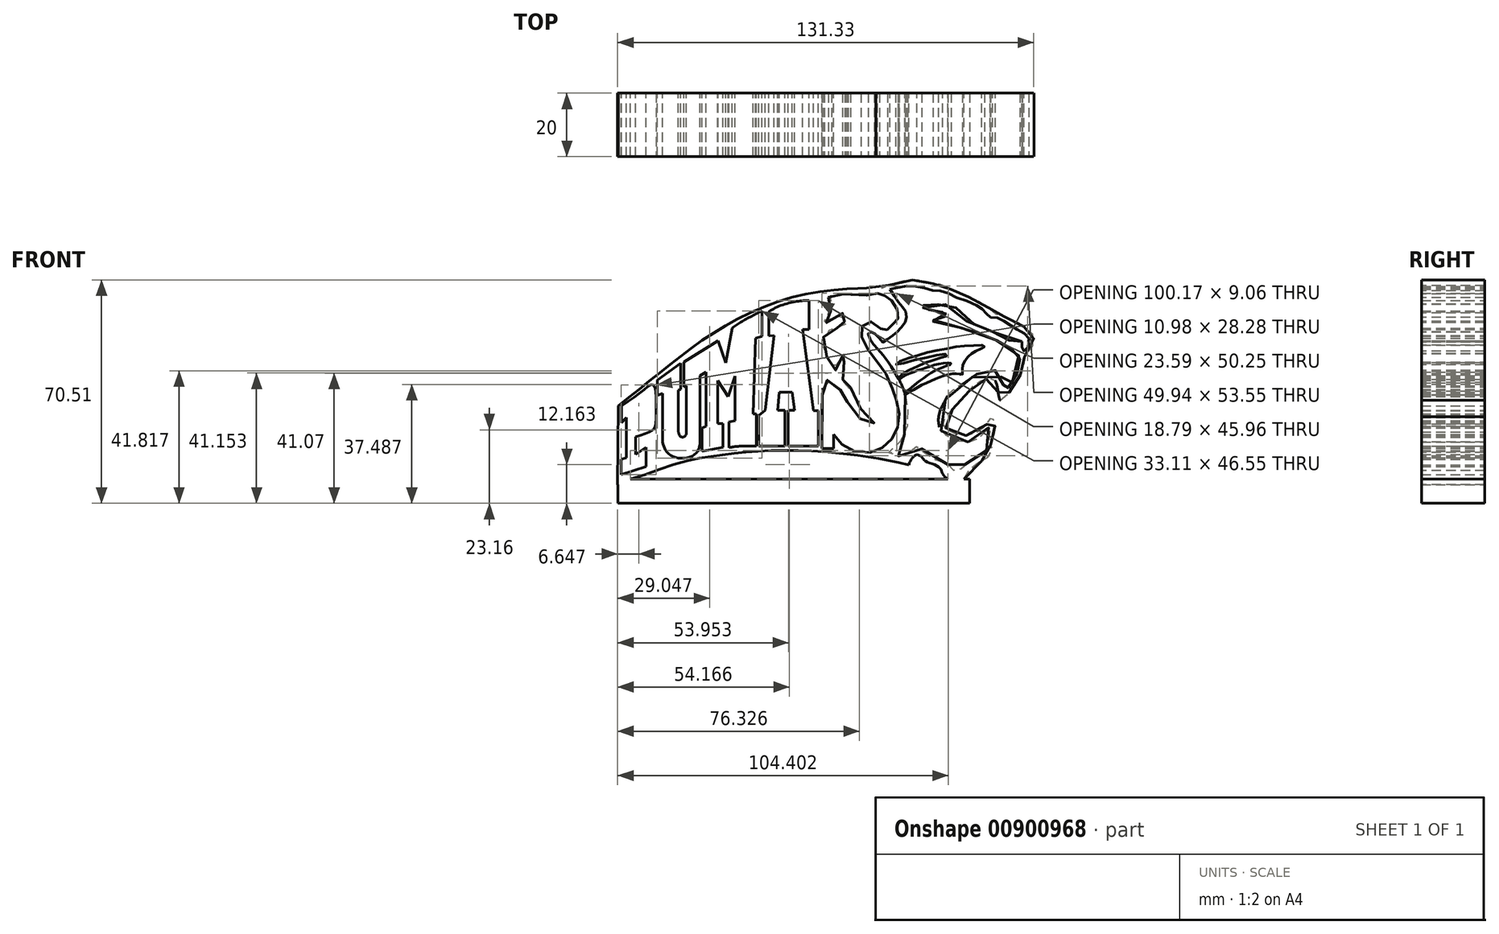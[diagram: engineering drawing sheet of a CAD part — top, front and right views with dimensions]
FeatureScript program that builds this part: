
annotation { "Feature Type Name" : "Feature", "Feature Type Description" : "" }
export const myFeature = defineFeature(function(context is Context, id is Id, definition is map)
    precondition{}
    {
        {
            var Q0;
            Q0=qCreatedBy(makeId("Front.planeOp"),FACE);
            var sketch = newSketch(context, id + "F0", { "sketchPlane" : qUnion([Q0])});
            skFitSpline(sketch, "E0", {"points": [v(-68.58, -24.03) * mm, v(-51.3, -10.22) * mm, v(-32, 2.86) * mm, v(-6.84, 11.75) * mm, v(10.19, 13.22) * mm, v(12.64, 13.54) * mm], "startDerivative": vector(74.63, 59.26) * mm, "endDerivative": vector(24.6, 4.5) * mm});
            skLineSegment(sketch, "E1", {"start": v(-68.58, -24.03) * mm, "end": v(-68.84, -49) * mm});
            skLineSegment(sketch, "E2", {"start": v(-68.84, -49) * mm, "end": v(-67.28, -47.87) * mm});
            skFitSpline(sketch, "E3", {"points": [v(-67.28, -47.87) * mm, v(-48.83, -41.9) * mm, v(-35.92, -39.57) * mm, v(-23.47, -38.32) * mm, v(-7.9, -38.32) * mm, v(4.23, -39.41) * mm, v(14.04, -40.81) * mm, v(23.06, -42.68) * mm], "startDerivative": vector(106.16, 25.81) * mm, "endDerivative": vector(73.73, -16.37) * mm});
            skArc(sketch, "E4", {"start": v(25.56, -39.43) * mm, "mid": v(23.95, -40.78) * mm, "end": v(23.06, -42.68) * mm});
            skFitSpline(sketch, "E5", {"points": [v(25.56, -39.43) * mm, v(27.14, -40.25) * mm, v(28.08, -41.39) * mm, v(32.57, -43.41) * mm, v(33.65, -45.3) * mm, v(36.03, -47.5) * mm, v(40.5, -47.12) * mm, v(42.59, -43.56) * mm, v(46.33, -41.4) * mm, v(49.38, -38.54) * mm, v(49.25, -36.83) * mm, v(48.76, -36.47) * mm, v(49.6, -34.71) * mm, v(50.35, -31.46) * mm, v(49.95, -29.08) * mm, v(49.12, -27.46) * mm, v(48.28, -29.04) * mm, v(45.11, -32.08) * mm, v(42.52, -33.26) * mm, v(39, -33.3) * mm, v(36.36, -32.38) * mm, v(34.34, -30.71) * mm, v(33.72, -29) * mm, v(36.18, -25.74) * mm, v(39.66, -22.27) * mm, v(41.63, -20) * mm, v(43.1, -18.07) * mm, v(45.12, -16.45) * mm, v(48.2, -15.36) * mm, v(49.6, -15.36) * mm, v(50.92, -17.84) * mm, v(51.92, -22.33) * mm, v(53.08, -21.4) * mm, v(54.66, -19.89) * mm, v(56.55, -17.7) * mm, v(57.96, -15.42) * mm, v(58.7, -12.56) * mm, v(59.39, -10.82) * mm, v(59.22, -9.2) * mm, v(61.34, -6.7) * mm, v(62.28, -4.5) * mm, v(62.36, -2.16) * mm, v(60.96, -0.33) * mm, v(60.29, 0) * mm, v(59.52, 0.7) * mm, v(57.94, 1.95) * mm, v(54.8, 3.39) * mm, v(52.07, 4.49) * mm, v(49.6, 5.2) * mm, v(48.89, 6.11) * mm, v(46.62, 8.06) * mm, v(43.12, 9.8) * mm, v(41.56, 10.52) * mm, v(39.68, 11.3) * mm, v(37.4, 12.2) * mm, v(35.53, 13.25) * mm, v(34.3, 14.02) * mm, v(31.83, 14.35) * mm, v(28.91, 15.06) * mm, v(27.1, 15.58) * mm, v(23.4, 15.58) * mm, v(19.38, 15) * mm, v(16.65, 14.02) * mm, v(14.82, 13.02) * mm, v(14.31, 13.2) * mm, v(13.98, 13.58) * mm, v(12.64, 13.54) * mm], "startDerivative": vector(143.2, -53.66) * mm, "endDerivative": vector(-143.74, -24.22) * mm});
            skLineSegment(sketch, "E6", {"start": v(-67.62, -24.03) * mm, "end": v(-67.62, -29.35) * mm});
            skLineSegment(sketch, "E7", {"start": v(-67.62, -29.35) * mm, "end": v(-66.13, -27.7) * mm});
            skLineSegment(sketch, "E8", {"start": v(-66.13, -27.7) * mm, "end": v(-66.13, -40.43) * mm});
            skLineSegment(sketch, "E9", {"start": v(-66.13, -40.43) * mm, "end": v(-67.68, -40.95) * mm});
            skLineSegment(sketch, "E10", {"start": v(-67.68, -40.95) * mm, "end": v(-67.68, -45.81) * mm});
            skLineSegment(sketch, "E11", {"start": v(-67.68, -45.81) * mm, "end": v(-59.92, -43.21) * mm});
            skLineSegment(sketch, "E12", {"start": v(-59.92, -43.21) * mm, "end": v(-59.92, -37.1) * mm});
            skLineSegment(sketch, "E13", {"start": v(-59.92, -37.1) * mm, "end": v(-63.16, -39.45) * mm});
            skLineSegment(sketch, "E14", {"start": v(-63.16, -39.45) * mm, "end": v(-63.16, -33.9) * mm});
            skFitSpline(sketch, "E15", {"points": [v(-63.16, -33.9) * mm, v(-58.76, -32.32) * mm, v(-57.3, -31.25) * mm, v(-56.8, -29.54) * mm, v(-56.73, -25.04) * mm, v(-56.86, -19.15) * mm, v(-57.43, -17.7) * mm, v(-58.06, -17.32) * mm, v(-60.02, -18.58) * mm, v(-67.62, -24.03) * mm], "startDerivative": vector(36.82, 11.88) * mm, "endDerivative": vector(-46.41, -30.43) * mm});
            skLineSegment(sketch, "E16", {"start": v(-56.35, -15.94) * mm, "end": v(-48.94, -10.66) * mm});
            skLineSegment(sketch, "E17", {"start": v(-48.94, -10.66) * mm, "end": v(-48.94, -18.9) * mm});
            skPoint(sketch, "E18.1.internal.orphan", {"position": v(-49.66, -31.77) * mm});
            skPoint(sketch, "E19.end.orphan", {"position": v(-49.66, -19.05) * mm});
            skLineSegment(sketch, "E20", {"start": v(-48.94, -18.9) * mm, "end": v(-49.66, -19.18) * mm});
            skLineSegment(sketch, "E21", {"start": v(-49.66, -19.18) * mm, "end": v(-49.66, -32.3) * mm});
            skFitSpline(sketch, "E22", {"points": [v(-49.66, -32.3) * mm, v(-49.39, -33.27) * mm, v(-48.87, -33.82) * mm, v(-47.94, -33.9) * mm, v(-47.22, -33.03) * mm, v(-47.19, -32.3) * mm], "startDerivative": vector(1.57, -3.84) * mm, "endDerivative": vector(-0.41, 3.84) * mm});
            skLineSegment(sketch, "E23", {"start": v(-47.19, -32.3) * mm, "end": v(-47.19, -17.66) * mm});
            skLineSegment(sketch, "E24", {"start": v(-47.19, -17.66) * mm, "end": v(-47.94, -18.12) * mm});
            skLineSegment(sketch, "E25", {"start": v(-47.94, -18.12) * mm, "end": v(-47.94, -10.21) * mm});
            skLineSegment(sketch, "E26", {"start": v(-47.94, -10.21) * mm, "end": v(-37.14, -3.5) * mm});
            skLineSegment(sketch, "E27", {"start": v(-37.14, -3.5) * mm, "end": v(-34.7, -10.49) * mm});
            skLineSegment(sketch, "E28", {"start": v(-34.7, -10.49) * mm, "end": v(-32.66, 0.5) * mm});
            skLineSegment(sketch, "E29", {"start": v(-56.35, -15.94) * mm, "end": v(-56.35, -20.78) * mm});
            skLineSegment(sketch, "E30", {"start": v(-56.35, -20.78) * mm, "end": v(-54.65, -20.17) * mm});
            skLineSegment(sketch, "E31", {"start": v(-54.65, -20.17) * mm, "end": v(-54.65, -35.54) * mm});
            skFitSpline(sketch, "E32", {"points": [v(-54.65, -35.54) * mm, v(-53.63, -38.17) * mm, v(-50.4, -40.38) * mm, v(-45.39, -39.96) * mm, v(-43.18, -37.66) * mm, v(-42.84, -35.54) * mm], "startDerivative": vector(3.7, -14.8) * mm, "endDerivative": vector(0.48, 13.21) * mm});
            skLineSegment(sketch, "E33", {"start": v(-42.84, -35.54) * mm, "end": v(-42.84, -14.55) * mm});
            skLineSegment(sketch, "E34", {"start": v(-42.84, -14.55) * mm, "end": v(-40.9, -13.39) * mm});
            skLineSegment(sketch, "E35", {"start": v(-40.9, -13.39) * mm, "end": v(-40.9, -30.6) * mm});
            skLineSegment(sketch, "E36", {"start": v(-40.9, -30.6) * mm, "end": v(-42.18, -31.08) * mm});
            skLineSegment(sketch, "E37", {"start": v(-42.18, -31.08) * mm, "end": v(-42.18, -38.47) * mm});
            skLineSegment(sketch, "E38", {"start": v(-42.18, -38.47) * mm, "end": v(-35.66, -37.1) * mm});
            skLineSegment(sketch, "E39", {"start": v(-35.66, -37.1) * mm, "end": v(-35.66, -29.67) * mm});
            skLineSegment(sketch, "E40", {"start": v(-35.66, -29.67) * mm, "end": v(-37.32, -29.67) * mm});
            skLineSegment(sketch, "E41", {"start": v(-37.32, -29.67) * mm, "end": v(-37.32, -16.07) * mm});
            skLineSegment(sketch, "E42", {"start": v(-37.32, -16.07) * mm, "end": v(-33.92, -21.1) * mm});
            skLineSegment(sketch, "E43", {"start": v(-33.92, -21.1) * mm, "end": v(-31.8, -14.72) * mm});
            skLineSegment(sketch, "E44", {"start": v(-31.8, -14.72) * mm, "end": v(-31.8, -28.74) * mm});
            skLineSegment(sketch, "E45", {"start": v(-31.8, -28.74) * mm, "end": v(-33.76, -29.14) * mm});
            skLineSegment(sketch, "E46", {"start": v(-33.76, -29.14) * mm, "end": v(-33.76, -36.74) * mm});
            skLineSegment(sketch, "E47", {"start": v(-25.07, -36.74) * mm, "end": v(-25.07, -26.63) * mm});
            skLineSegment(sketch, "E48", {"start": v(-25.07, -26.63) * mm, "end": v(-26.1, -26.63) * mm});
            skLineSegment(sketch, "E49", {"start": v(-26.1, -26.63) * mm, "end": v(-25.35, -2.78) * mm});
            skLineSegment(sketch, "E50", {"start": v(-25.35, -2.78) * mm, "end": v(-23.24, -2.04) * mm});
            skLineSegment(sketch, "E51", {"start": v(-23.24, -2.04) * mm, "end": v(-23.24, 5.93) * mm});
            skFitSpline(sketch, "E52", {"points": [v(-32.66, 0.5) * mm, v(-29.73, 2.5) * mm, v(-26.17, 4.46) * mm, v(-23.24, 5.93) * mm], "startDerivative": vector(9.2, 7.58) * mm, "endDerivative": vector(8.34, 3.6) * mm});
            skFitSpline(sketch, "E53", {"points": [v(-21.15, 5.7) * mm, v(-17.85, 7.43) * mm, v(-13.71, 8.67) * mm, v(-10.4, 9.15) * mm, v(-8.4, 9.22) * mm], "startDerivative": vector(11.86, 6.88) * mm, "endDerivative": vector(9.68, 0.1) * mm});
            skLineSegment(sketch, "E54", {"start": v(-21.15, 5.7) * mm, "end": v(-21.15, -2) * mm});
            skLineSegment(sketch, "E55", {"start": v(-21.15, -2) * mm, "end": v(-19.43, -1.87) * mm});
            skLineSegment(sketch, "E56", {"start": v(-19.43, -1.87) * mm, "end": v(-22.34, -25.41) * mm});
            skLineSegment(sketch, "E57", {"start": v(-22.34, -25.41) * mm, "end": v(-24.28, -27.17) * mm});
            skLineSegment(sketch, "E58", {"start": v(-24.28, -27.17) * mm, "end": v(-24.28, -36.74) * mm});
            skLineSegment(sketch, "E59", {"start": v(-24.28, -36.74) * mm, "end": v(-16.07, -36.74) * mm});
            skLineSegment(sketch, "E60", {"start": v(-16.07, -36.74) * mm, "end": v(-16.07, -25.48) * mm});
            skLineSegment(sketch, "E61", {"start": v(-16.07, -25.48) * mm, "end": v(-18.3, -25.48) * mm});
            skLineSegment(sketch, "E62", {"start": v(-18.3, -25.48) * mm, "end": v(-17.86, -19.79) * mm});
            skLineSegment(sketch, "E63", {"start": v(-17.86, -19.79) * mm, "end": v(-13.72, -19.79) * mm});
            skLineSegment(sketch, "E64", {"start": v(-13.72, -19.79) * mm, "end": v(-13.03, -25.41) * mm});
            skLineSegment(sketch, "E65", {"start": v(-13.03, -25.41) * mm, "end": v(-15.04, -25.48) * mm});
            skLineSegment(sketch, "E66", {"start": v(-15.04, -25.48) * mm, "end": v(-15.04, -36.74) * mm});
            skLineSegment(sketch, "E67", {"start": v(-15.04, -36.74) * mm, "end": v(-5.5, -36.74) * mm});
            skLineSegment(sketch, "E68", {"start": v(-5.5, -36.74) * mm, "end": v(-5.5, -25.54) * mm});
            skLineSegment(sketch, "E69", {"start": v(-5.5, -25.54) * mm, "end": v(-7.1, -25.54) * mm});
            skFitSpline(sketch, "E70", {"points": [v(-25.07, -36.74) * mm, v(-28.76, -36.74) * mm, v(-31.67, -36.94) * mm, v(-33.75, -37.26) * mm], "startDerivative": vector(-9.97, 0.12) * mm, "endDerivative": vector(-7.01, -1.22) * mm});
            skLineSegment(sketch, "E71", {"start": v(-33.76, -36.74) * mm, "end": v(-33.75, -37.26) * mm});
            skLineSegment(sketch, "E72", {"start": v(-7.1, -25.54) * mm, "end": v(-10.5, 0) * mm});
            skLineSegment(sketch, "E73", {"start": v(-10.5, 0) * mm, "end": v(-8.43, 0) * mm});
            skLineSegment(sketch, "E74", {"start": v(-8.43, 0) * mm, "end": v(-8.4, 9.22) * mm});
            skFitSpline(sketch, "E75", {"points": [v(13.11, 11.45) * mm, v(13.53, 10.85) * mm, v(13.75, 10.21) * mm, v(12.18, 10.29) * mm, v(9.42, 10.92) * mm, v(8.33, 11.22) * mm, v(5.3, 11.22) * mm, v(1.31, 11.26) * mm, v(0, 11.22) * mm, v(-0.9, 10.9) * mm, v(-1.92, 10.58) * mm, v(-2.34, 10.16) * mm, v(-2.34, 9.35) * mm, v(-1.89, 8.52) * mm, v(-1.44, 8.03) * mm, v(-1.37, 6.65) * mm, v(-2.3, 5) * mm, v(-3.3, 3.53) * mm, v(-3.62, 2.66) * mm, v(-3.34, 2.2) * mm, v(-2.43, 2.37) * mm, v(-0.6, 3.66) * mm, v(1.17, 4.69) * mm, v(2.3, 5.2) * mm, v(3.46, 5.2) * mm, v(2.55, 3.98) * mm, v(2.17, 3.17) * mm, v(2.52, 2.56) * mm, v(3.65, 2.47) * mm, v(3.87, 2.24) * mm, v(3.42, 1.82) * mm, v(1.78, 1.18) * mm, v(-0.37, 0.31) * mm, v(-1.7, 0) * mm, v(-3.34, -1.17) * mm, v(-3.88, -2.2) * mm, v(-4.05, -4.44) * mm, v(-4, -5.75) * mm, v(-3, -8.2) * mm, v(-1.99, -10.44) * mm, v(-0.56, -12.96) * mm, v(-0.25, -13.28) * mm, v(0, -12.73) * mm, v(0.27, -11.46) * mm, v(0.7, -10.24) * mm, v(1.33, -9.15) * mm, v(2.18, -8.22) * mm, v(2.6, -7.84) * mm, v(2.88, -7.66) * mm, v(3.1, -7.63) * mm, v(3.2, -8.1) * mm, v(2.83, -9.4) * mm, v(2.45, -11) * mm, v(2.24, -12.43) * mm, v(2.09, -13.8) * mm, v(2.24, -15.85) * mm, v(2.61, -16.7) * mm, v(3.45, -16.7) * mm, v(4.24, -16.8) * mm, v(4.59, -17.08) * mm, v(4.62, -18.8) * mm, v(5.66, -21.42) * mm, v(7.12, -24.06) * mm, v(9.31, -26.76) * mm, v(10.72, -28) * mm, v(11.78, -29.07) * mm, v(12.18, -29.74) * mm, v(11.5, -29.9) * mm, v(9.99, -29.46) * mm, v(8.52, -28.73) * mm, v(6.67, -27.21) * mm, v(5.1, -25.58) * mm, v(3.91, -23.5) * mm, v(3.24, -21.98) * mm, v(2.85, -20.8) * mm, v(2.7, -19.5) * mm, v(1.93, -19.28) * mm, v(0.9, -18.54) * mm, v(-0.62, -17.27) * mm, v(-1.57, -16.56) * mm, v(-2.52, -15.96) * mm, v(-3.34, -15.82) * mm, v(-3.97, -15.86) * mm, v(-4.11, -17.62) * mm, v(-4.26, -21.77) * mm, v(-4.31, -37.52) * mm], "startDerivative": vector(46.68, -64.88) * mm, "endDerivative": vector(16.15, -484.38) * mm});
            skLineSegment(sketch, "E76", {"start": v(-4.31, -37.52) * mm, "end": v(-0.66, -37.52) * mm});
            skLineSegment(sketch, "E77", {"start": v(-0.66, -37.52) * mm, "end": v(-0.66, -33.04) * mm});
            skFitSpline(sketch, "E78", {"points": [v(-0.66, -33.04) * mm, v(1.25, -35.45) * mm, v(3.66, -37.51) * mm, v(7.93, -38.77) * mm, v(11.75, -38.57) * mm, v(14.56, -37.41) * mm, v(17.03, -35.45) * mm, v(18.48, -33.04) * mm, v(19.69, -30.08) * mm, v(20.04, -26.81) * mm, v(19.49, -23.6) * mm, v(18.58, -20.33) * mm, v(17.63, -17.97) * mm, v(15.54, -13.52) * mm, v(13.22, -10.28) * mm, v(10.81, -7.3) * mm, v(8.86, -3.97) * mm, v(7.93, -1) * mm, v(8.27, 0.85) * mm, v(9.6, 2.43) * mm, v(11.58, 2.4) * mm, v(13.68, 0.96) * mm, v(15.27, -0.78) * mm, v(15.65, -0.59) * mm, v(16.74, 0.54) * mm, v(17.53, 1.36) * mm, v(18.52, 2.22) * mm, v(19.59, 3.03) * mm, v(19.65, 3.52) * mm, v(19.65, 4.92) * mm, v(19.41, 6.41) * mm, v(18.44, 8.4) * mm, v(17.28, 9.51) * mm, v(16.26, 10.27) * mm, v(15.24, 10.89) * mm, v(14.13, 11.26) * mm, v(13.11, 11.45) * mm], "startDerivative": vector(57.68, -76.4) * mm, "endDerivative": vector(-53.68, 8.07) * mm});
            skFitSpline(sketch, "E79", {"points": [v(17.08, 12.72) * mm, v(19.2, 9.55) * mm, v(20.78, 7.4) * mm, v(22.08, 5.74) * mm, v(22.3, 3.72) * mm, v(21.72, 2.13) * mm, v(19.92, 0) * mm, v(18.7, -1.32) * mm, v(16.53, -2.84) * mm, v(14.8, -3.99) * mm, v(13.5, -2.48) * mm, v(12.14, -1.25) * mm, v(10.98, -0.75) * mm, v(10.26, -0.96) * mm, v(10.7, -2.9) * mm, v(12, -4.78) * mm, v(14.01, -6.94) * mm, v(16.42, -10.1) * mm, v(17.6, -11.78) * mm, v(19.11, -14.24) * mm, v(20.99, -17.9) * mm, v(21.85, -20.36) * mm, v(22.5, -22.73) * mm, v(22.71, -25.68) * mm, v(22.64, -28.06) * mm, v(22.5, -30.43) * mm, v(21.49, -33.38) * mm, v(20.1, -35.89) * mm, v(18.48, -37.8) * mm, v(16.38, -39.14) * mm, v(17.68, -39.62) * mm, v(19.66, -39.92) * mm, v(21.68, -40.4) * mm, v(22.16, -39.88) * mm, v(23.13, -38.5) * mm, v(24.1, -37.57) * mm, v(25.3, -36.93) * mm, v(26.64, -37.12) * mm, v(27.38, -37.98) * mm, v(28.54, -39.17) * mm, v(29.8, -40.1) * mm, v(31.38, -41) * mm, v(33.02, -41.49) * mm, v(34.77, -42.02) * mm, v(35.52, -42.83) * mm, v(35.63, -43.54) * mm, v(36.6, -44.12) * mm, v(37.45, -44.4) * mm, v(38.27, -44.45) * mm, v(38.87, -44.4) * mm, v(39.55, -43.93) * mm, v(39.91, -43.6) * mm, v(40.48, -42.76) * mm, v(42, -41.72) * mm, v(43.43, -41.04) * mm, v(44.8, -40.29) * mm, v(45.66, -39.9) * mm, v(46.47, -39.9) * mm, v(47.14, -39.3) * mm, v(47.52, -38.45) * mm, v(47.83, -36.83) * mm, v(48.3, -35.19) * mm, v(48.58, -33.93) * mm, v(48.76, -32.6) * mm, v(48.76, -31.3) * mm, v(48.76, -30.64) * mm, v(48.58, -30.56) * mm, v(48.15, -31.06) * mm, v(47.53, -31.76) * mm, v(46.67, -32.8) * mm, v(45.8, -33.68) * mm, v(44.67, -34.71) * mm, v(43.8, -35.14) * mm, v(43.17, -35.36) * mm, v(41.86, -35.47) * mm, v(40.53, -35.43) * mm, v(39.17, -35.33) * mm, v(37.9, -35.04) * mm, v(36.03, -34.3) * mm, v(34.52, -33.04) * mm, v(33.71, -32.48) * mm, v(32.86, -31.14) * mm, v(32.5, -29.74) * mm, v(32.41, -27.73) * mm, v(33.02, -25.37) * mm, v(33.84, -23.6) * mm, v(34.5, -22.45) * mm, v(35.94, -20) * mm, v(37.87, -18.48) * mm, v(39.15, -17.53) * mm, v(40.58, -17.04) * mm, v(41.94, -15.84) * mm, v(43.68, -14.52) * mm, v(45.41, -13.61) * mm, v(47.63, -13.08) * mm, v(49.6, -12.93) * mm, v(51.03, -13.05) * mm, v(52.07, -14.67) * mm, v(52.69, -16.45) * mm, v(53.03, -18.14) * mm, v(53.06, -19.04) * mm, v(53.19, -19.4) * mm, v(53.6, -19.4) * mm, v(54.02, -18.9) * mm, v(55, -17.7) * mm, v(55.9, -16.45) * mm, v(56.86, -14.56) * mm, v(57.37, -13.25) * mm, v(57.88, -11.8) * mm, v(58.06, -10.56) * mm, v(58.1, -9.5) * mm, v(57.9, -8.52) * mm, v(57.44, -7.92) * mm, v(56.55, -7.12) * mm, v(55.9, -6.4) * mm, v(54.79, -5.64) * mm, v(53.68, -4.94) * mm, v(52.07, -4.05) * mm, v(50.55, -3.34) * mm, v(48.44, -2.36) * mm, v(46.74, -1.76) * mm, v(44.81, -0.99) * mm, v(42.94, -0.37) * mm, v(40.1, 0.44) * mm, v(38.87, 0.82) * mm, v(37.21, 1.27) * mm, v(35.58, 1.74) * mm, v(34.27, 2.1) * mm, v(32.56, 2.45) * mm, v(31.6, 2.63) * mm, v(30.7, 2.63) * mm, v(30.95, 3.1) * mm, v(31.8, 3.45) * mm, v(32.53, 3.65) * mm, v(33.27, 3.83) * mm, v(34.05, 4.03) * mm, v(34.62, 4.1) * mm, v(35.09, 4.3) * mm, v(35.35, 4.49) * mm, v(35.31, 4.74) * mm, v(34.71, 5.07) * mm, v(33.86, 5.46) * mm, v(33.05, 5.78) * mm, v(31.92, 6.1) * mm, v(30.75, 6.26) * mm, v(29.7, 6.3) * mm, v(28.86, 6.47) * mm, v(28.1, 6.7) * mm, v(27.52, 6.97) * mm, v(27.14, 7.2) * mm, v(27.42, 7.53) * mm, v(28.06, 7.77) * mm, v(29.04, 7.9) * mm, v(29.6, 7.97) * mm, v(31.25, 7.97) * mm, v(33.05, 8) * mm, v(35.06, 7.92) * mm, v(37.04, 7.26) * mm, v(38.62, 6.66) * mm, v(39.87, 5.8) * mm, v(40.51, 5) * mm, v(40.93, 4.24) * mm, v(41.21, 3.18) * mm, v(41.3, 2.3) * mm, v(41.51, 2.25) * mm, v(42.36, 2.06) * mm, v(43.8, 1.59) * mm, v(45.8, 1) * mm, v(48.2, 0) * mm, v(50.26, -1.04) * mm, v(52.92, -2.55) * mm, v(54.14, -3.13) * mm, v(54.86, -3.42) * mm, v(55.78, -3.56) * mm, v(57.19, -3.7) * mm, v(58.2, -3.7) * mm, v(58.7, -3.7) * mm], "startDerivative": vector(235.65, -353.26) * mm, "endDerivative": vector(181.98, -57.59) * mm});
            skFitSpline(sketch, "E80", {"points": [v(58.7, -3.7) * mm, v(58.83, -3.9) * mm, v(58.82, -4.4) * mm, v(58.8, -5.4) * mm, v(58.82, -6.3) * mm, v(58.84, -6.62) * mm, v(59.03, -6.77) * mm, v(59.4, -6.78) * mm, v(59.7, -6.6) * mm, v(60.23, -6.1) * mm, v(60.66, -5.5) * mm, v(60.84, -4.01) * mm, v(60.84, -2.72) * mm, v(60.57, -1.93) * mm, v(60.06, -1.54) * mm, v(58.95, -1.03) * mm, v(57.9, -0.43) * mm, v(56.96, 0.26) * mm, v(56.36, 0.65) * mm, v(55.27, 1.29) * mm, v(54.34, 1.89) * mm, v(53.29, 2.55) * mm, v(52.32, 3.12) * mm, v(51.48, 3.51) * mm, v(50.9, 3.72) * mm, v(50.12, 3.84) * mm, v(49.17, 3.93) * mm, v(48.62, 3.93) * mm, v(48.32, 4.1) * mm, v(47.92, 4.5) * mm, v(47.4, 5.2) * mm, v(46.78, 5.8) * mm, v(46.4, 6.31) * mm, v(45.79, 6.8) * mm, v(44.8, 7.43) * mm, v(44.36, 7.72) * mm, v(42.5, 8.8) * mm, v(40.64, 9.22) * mm, v(38.7, 9.84) * mm, v(37.25, 10.46) * mm, v(35.87, 11.3) * mm, v(34, 11.92) * mm, v(33.37, 12.16) * mm, v(31.98, 12.2) * mm, v(31.07, 12.23) * mm, v(30.32, 12.39) * mm, v(29.09, 12.78) * mm, v(27.86, 13.23) * mm, v(26.36, 13.52) * mm, v(25.3, 13.72) * mm, v(23.93, 13.91) * mm, v(22.08, 13.75) * mm, v(20.33, 13.43) * mm, v(19.02, 13.12) * mm, v(17.78, 12.93) * mm, v(17.08, 12.72) * mm], "startDerivative": vector(16.92, -18.68) * mm, "endDerivative": vector(-40.47, -14.97) * mm});
            skFitSpline(sketch, "E81", {"points": [v(46.08, -4.94) * mm, v(46.56, -4.93) * mm, v(46.93, -5.32) * mm, v(46.58, -5.76) * mm, v(45.67, -6.13) * mm, v(44.45, -6.63) * mm, v(43.34, -7.28) * mm, v(42.64, -7.7) * mm, v(41.9, -8.35) * mm, v(41.2, -9.04) * mm, v(40.7, -9.92) * mm, v(40.18, -10.85) * mm, v(40, -11.78) * mm, v(39.95, -12.48) * mm, v(39.95, -13.31) * mm, v(39.9, -14.33) * mm, v(39.5, -14.26) * mm, v(39.16, -14.06) * mm, v(38.74, -13.92) * mm, v(37.89, -13.92) * mm, v(37.57, -13.89) * mm, v(36.86, -13.98) * mm, v(36.11, -14.12) * mm, v(35.32, -14.25) * mm, v(34.39, -14.49) * mm, v(33.24, -14.91) * mm, v(32.66, -15.07) * mm, v(31.78, -15.44) * mm, v(30.88, -15.79) * mm, v(30.03, -16.19) * mm, v(29.1, -16.61) * mm, v(28.04, -17.12) * mm, v(27.08, -17.57) * mm, v(26.18, -18.07) * mm, v(25.38, -18.47) * mm, v(24.64, -18.92) * mm, v(23.74, -19.48) * mm, v(22.75, -20.1) * mm, v(21.96, -20.7) * mm, v(21.8, -20.2) * mm, v(22.36, -19.51) * mm, v(23.15, -18.88) * mm, v(23.97, -18.21) * mm, v(24.92, -17.45) * mm, v(25.65, -16.83) * mm], "startDerivative": vector(27.78, 5.61) * mm, "endDerivative": vector(29.47, 24.84) * mm});
            skFitSpline(sketch, "E82", {"points": [v(25.65, -16.83) * mm, v(26.23, -16.39) * mm, v(26.83, -15.88) * mm, v(27.54, -15.37) * mm, v(28.32, -14.82) * mm, v(29.15, -14.22) * mm, v(29.96, -13.72) * mm, v(30.58, -13.35) * mm, v(31.36, -12.93) * mm, v(32.3, -12.5) * mm, v(33.25, -12.08) * mm, v(34.01, -11.8) * mm, v(34.65, -11.54) * mm, v(35.23, -11.3) * mm, v(35.72, -11.18) * mm, v(36.17, -11.03) * mm, v(36.4, -10.88) * mm, v(36.4, -10.66) * mm, v(36.19, -10.51) * mm, v(35.76, -10.47) * mm, v(34.97, -10.45) * mm, v(33.9, -10.6) * mm, v(32.66, -10.8) * mm, v(32, -10.98) * mm, v(31.14, -11.15) * mm, v(30.2, -11.47) * mm, v(29.26, -11.73) * mm, v(28.5, -11.99) * mm, v(27.45, -12.35) * mm, v(26.6, -12.58) * mm, v(25.85, -12.82) * mm, v(25.06, -13.12) * mm, v(24.2, -13.5) * mm, v(23.65, -13.7) * mm, v(22.8, -13.98) * mm, v(21.94, -14.4) * mm, v(21.37, -14.76) * mm, v(20.6, -15.32) * mm, v(20, -15.84) * mm, v(19.75, -15.37) * mm, v(19.96, -15) * mm, v(20.25, -14.6) * mm, v(20.86, -13.98) * mm, v(21.92, -13.42) * mm, v(22.86, -12.95) * mm, v(24.1, -12.42) * mm, v(24.86, -12.07) * mm, v(25.65, -11.63) * mm, v(26.63, -11.19) * mm, v(27.77, -10.66) * mm, v(28.89, -10.27) * mm, v(29.83, -9.98) * mm, v(30.74, -9.66) * mm, v(31.71, -9.33) * mm, v(32.66, -8.98) * mm, v(33.53, -8.72) * mm, v(34.39, -8.48) * mm, v(34.92, -8.3) * mm, v(35.22, -8.17) * mm, v(35.36, -7.98) * mm, v(35.26, -7.78) * mm, v(34.86, -7.72) * mm, v(33.93, -7.76) * mm, v(33, -7.86) * mm, v(31.46, -8.2) * mm, v(29.76, -8.51) * mm, v(28, -8.94) * mm, v(25.32, -9.47) * mm, v(23.24, -10.06) * mm, v(21.52, -10.56) * mm, v(19.93, -11.05) * mm, v(19.37, -11.05) * mm, v(18.94, -10.99) * mm, v(18.87, -10.64) * mm, v(19.44, -10.3) * mm, v(20.42, -9.9) * mm, v(21.7, -9.46) * mm, v(23.16, -8.99) * mm, v(24.42, -8.62) * mm, v(26.25, -8.05) * mm, v(27.55, -7.63) * mm, v(28.89, -7.24) * mm, v(30.32, -6.94) * mm, v(31.92, -6.6) * mm, v(33.13, -6.3) * mm, v(34.77, -6.02) * mm, v(36.42, -5.77) * mm, v(37.76, -5.47) * mm, v(39.2, -5.36) * mm, v(40.06, -5.23) * mm, v(41.5, -5.16) * mm, v(42.74, -5.09) * mm, v(44.04, -4.92) * mm, v(45.24, -4.92) * mm, v(46.08, -4.94) * mm], "startDerivative": vector(62.23, 46.13) * mm, "endDerivative": vector(79.94, -1.41) * mm});
            skSolve(sketch);
        }
        {
            var Q0;
            Q0 = qSketchRegion(id + "F0", true);
            var Q1;
            {var subQ1=sQuery(id+"F0.wireOp",EDGE,"E81");Q1=makeQuery(id+"F0.imprint","IMPRINT",FACE,{"disambiguationData":[TD([[makeQuery(id+"F0.imprint","IMPRINT",EDGE,{"derivedFrom":subQ1}),-1.0]])]});}
            extrude(context, id + "F1", {"entities" : qUnion([Q0, Q1]), "depth" : 20 * mm, "offsetDistance" : 25 * mm});
        }
        {
            var Q0;
            Q0=makeQuery(id+"F1.opExtrude","CAP_FACE",FACE,{"disambiguationData":[OSD([sQuery(id+"F0.wireOp",EDGE,"E0"),sQuery(id+"F0.wireOp",EDGE,"E1"),sQuery(id+"F0.wireOp",EDGE,"E2"),sQuery(id+"F0.wireOp",EDGE,"E3"),sQuery(id+"F0.wireOp",EDGE,"E4"),sQuery(id+"F0.wireOp",EDGE,"E5"),sQuery(id+"F0.wireOp",EDGE,"E6"),sQuery(id+"F0.wireOp",EDGE,"E7"),sQuery(id+"F0.wireOp",EDGE,"E8"),sQuery(id+"F0.wireOp",EDGE,"E9"),sQuery(id+"F0.wireOp",EDGE,"E10"),sQuery(id+"F0.wireOp",EDGE,"E11"),sQuery(id+"F0.wireOp",EDGE,"E12"),sQuery(id+"F0.wireOp",EDGE,"E13"),sQuery(id+"F0.wireOp",EDGE,"E14"),sQuery(id+"F0.wireOp",EDGE,"E15"),sQuery(id+"F0.wireOp",EDGE,"E16"),sQuery(id+"F0.wireOp",EDGE,"E17"),sQuery(id+"F0.wireOp",EDGE,"E20"),sQuery(id+"F0.wireOp",EDGE,"E21"),sQuery(id+"F0.wireOp",EDGE,"E22"),sQuery(id+"F0.wireOp",EDGE,"E23"),sQuery(id+"F0.wireOp",EDGE,"E24"),sQuery(id+"F0.wireOp",EDGE,"E25"),sQuery(id+"F0.wireOp",EDGE,"E26"),sQuery(id+"F0.wireOp",EDGE,"E27"),sQuery(id+"F0.wireOp",EDGE,"E28"),sQuery(id+"F0.wireOp",EDGE,"E29"),sQuery(id+"F0.wireOp",EDGE,"E30"),sQuery(id+"F0.wireOp",EDGE,"E31"),sQuery(id+"F0.wireOp",EDGE,"E32"),sQuery(id+"F0.wireOp",EDGE,"E33"),sQuery(id+"F0.wireOp",EDGE,"E34"),sQuery(id+"F0.wireOp",EDGE,"E35"),sQuery(id+"F0.wireOp",EDGE,"E36"),sQuery(id+"F0.wireOp",EDGE,"E37"),sQuery(id+"F0.wireOp",EDGE,"E38"),sQuery(id+"F0.wireOp",EDGE,"E39"),sQuery(id+"F0.wireOp",EDGE,"E40"),sQuery(id+"F0.wireOp",EDGE,"E41"),sQuery(id+"F0.wireOp",EDGE,"E42"),sQuery(id+"F0.wireOp",EDGE,"E43"),sQuery(id+"F0.wireOp",EDGE,"E44"),sQuery(id+"F0.wireOp",EDGE,"E45"),sQuery(id+"F0.wireOp",EDGE,"E46"),sQuery(id+"F0.wireOp",EDGE,"E47"),sQuery(id+"F0.wireOp",EDGE,"E48"),sQuery(id+"F0.wireOp",EDGE,"E49"),sQuery(id+"F0.wireOp",EDGE,"E50"),sQuery(id+"F0.wireOp",EDGE,"E51"),sQuery(id+"F0.wireOp",EDGE,"E52"),sQuery(id+"F0.wireOp",EDGE,"E53"),sQuery(id+"F0.wireOp",EDGE,"E54"),sQuery(id+"F0.wireOp",EDGE,"E55"),sQuery(id+"F0.wireOp",EDGE,"E56"),sQuery(id+"F0.wireOp",EDGE,"E57"),sQuery(id+"F0.wireOp",EDGE,"E58"),sQuery(id+"F0.wireOp",EDGE,"E59"),sQuery(id+"F0.wireOp",EDGE,"E60"),sQuery(id+"F0.wireOp",EDGE,"E61"),sQuery(id+"F0.wireOp",EDGE,"E62"),sQuery(id+"F0.wireOp",EDGE,"E63"),sQuery(id+"F0.wireOp",EDGE,"E64"),sQuery(id+"F0.wireOp",EDGE,"E65"),sQuery(id+"F0.wireOp",EDGE,"E66"),sQuery(id+"F0.wireOp",EDGE,"E67"),sQuery(id+"F0.wireOp",EDGE,"E68"),sQuery(id+"F0.wireOp",EDGE,"E69"),sQuery(id+"F0.wireOp",EDGE,"E70"),sQuery(id+"F0.wireOp",EDGE,"E71"),sQuery(id+"F0.wireOp",EDGE,"E72"),sQuery(id+"F0.wireOp",EDGE,"E73"),sQuery(id+"F0.wireOp",EDGE,"E74"),sQuery(id+"F0.wireOp",EDGE,"E75"),sQuery(id+"F0.wireOp",EDGE,"E76"),sQuery(id+"F0.wireOp",EDGE,"E77"),sQuery(id+"F0.wireOp",EDGE,"E78"),sQuery(id+"F0.wireOp",EDGE,"E79"),sQuery(id+"F0.wireOp",EDGE,"E80"),sQuery(id+"F0.wireOp",EDGE,"E81"),sQuery(id+"F0.wireOp",EDGE,"E81"),sQuery(id+"F0.wireOp",EDGE,"E82"),sQuery(id+"F0.wireOp",EDGE,"E82")])],"isStart":false});
            var sketch = newSketch(context, id + "F2", { "sketchPlane" : qUnion([Q0])});
            skLineSegment(sketch, "E83.bottom", {"start": v(-68.82, -47.2) * mm, "end": v(42.23, -47.2) * mm});
            skLineSegment(sketch, "E83.top", {"start": v(-68.82, -54.83) * mm, "end": v(42.23, -54.83) * mm});
            skLineSegment(sketch, "E83.left", {"start": v(-68.82, -47.2) * mm, "end": v(-68.82, -54.83) * mm});
            skLineSegment(sketch, "E83.right", {"start": v(42.23, -47.2) * mm, "end": v(42.23, -54.83) * mm});
            skSolve(sketch);
        }
        {
            var Q0;
            Q0 = qSketchRegion(id + "F2", true);
            extrude(context, id + "F3", {"entities" : qUnion([Q0]), "operationType" : NewBodyOperationType.ADD, "oppositeDirection" : true, "depth" : 20 * mm, "offsetDistance" : 25 * mm});
        }
    });
